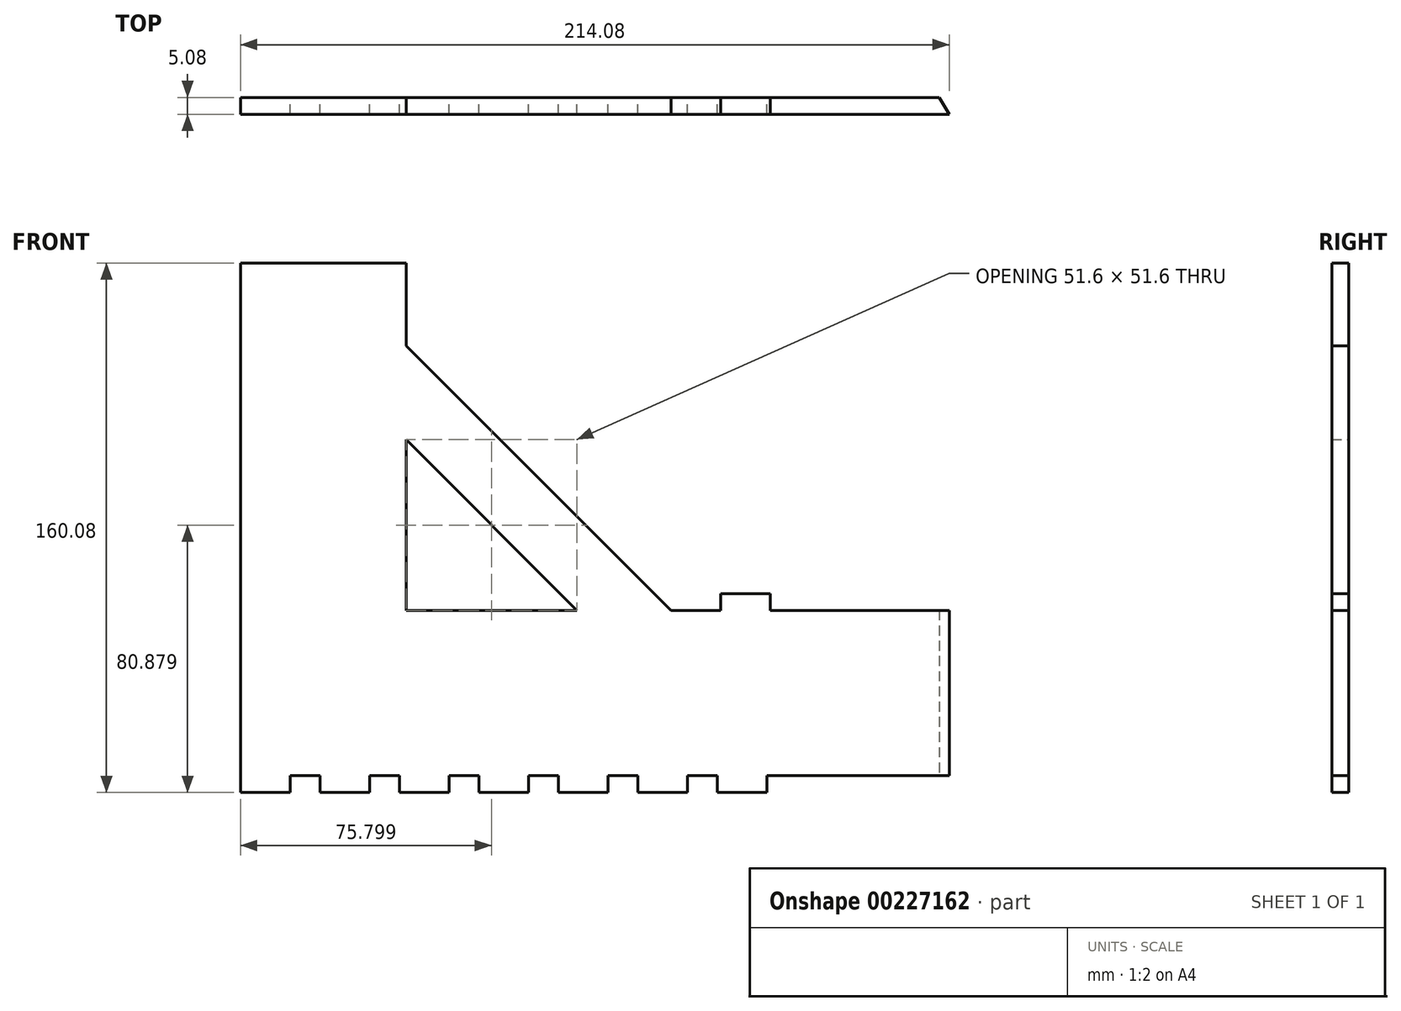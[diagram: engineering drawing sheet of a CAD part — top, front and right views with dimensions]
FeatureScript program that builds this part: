
annotation { "Feature Type Name" : "Feature", "Feature Type Description" : "" }
export const myFeature = defineFeature(function(context is Context, id is Id, definition is map)
    precondition{}
    {
        {
            var Q0;
            Q0=qCreatedBy(makeId("Front.planeOp"),FACE);
            var sketch = newSketch(context, id + "F0", { "sketchPlane" : qUnion([Q0])});
            skLineSegment(sketch, "E0", {"start": v(-32.42, 0) * mm, "end": v(-246.5, 0) * mm});
            skLineSegment(sketch, "E1", {"start": v(-246.5, 0) * mm, "end": v(-246.5, 130) * mm});
            skLineSegment(sketch, "E2", {"start": v(-246.5, 130) * mm, "end": v(-196.5, 130) * mm});
            skLineSegment(sketch, "E3", {"start": v(-196.5, 130) * mm, "end": v(-196.5, 50) * mm});
            skLineSegment(sketch, "E4", {"start": v(-196.5, 50) * mm, "end": v(-32.42, 50) * mm});
            skLineSegment(sketch, "E5", {"start": v(-196.5, 130) * mm, "end": v(-116.5, 50) * mm});
            skLineSegment(sketch, "E6", {"start": v(-196.5, 101.6) * mm, "end": v(-144.9, 50) * mm});
            skLineSegment(sketch, "E7", {"start": v(-246.5, 0) * mm, "end": v(-246.5, -5.08) * mm});
            skLineSegment(sketch, "E8", {"start": v(-246.5, -5.08) * mm, "end": v(-231.5, -5.08) * mm});
            skLineSegment(sketch, "E9", {"start": v(-231.5, -5.08) * mm, "end": v(-231.5, 0) * mm});
            skLineSegment(sketch, "E10.1.0.0", {"start": v(-207.5, -5.08) * mm, "end": v(-207.5, 0) * mm});
            skLineSegment(sketch, "E10.1.0.1", {"start": v(-222.5, -5.08) * mm, "end": v(-207.5, -5.08) * mm});
            skLineSegment(sketch, "E10.1.0.2", {"start": v(-222.5, 0) * mm, "end": v(-222.5, -5.08) * mm});
            skLineSegment(sketch, "E10.2.0.0", {"start": v(-183.5, -5.08) * mm, "end": v(-183.5, 0) * mm});
            skLineSegment(sketch, "E10.2.0.1", {"start": v(-198.5, -5.08) * mm, "end": v(-183.5, -5.08) * mm});
            skLineSegment(sketch, "E10.2.0.2", {"start": v(-198.5, 0) * mm, "end": v(-198.5, -5.08) * mm});
            skLineSegment(sketch, "E10.3.0.0", {"start": v(-159.5, -5.08) * mm, "end": v(-159.5, 0) * mm});
            skLineSegment(sketch, "E10.3.0.1", {"start": v(-174.5, -5.08) * mm, "end": v(-159.5, -5.08) * mm});
            skLineSegment(sketch, "E10.3.0.2", {"start": v(-174.5, 0) * mm, "end": v(-174.5, -5.08) * mm});
            skLineSegment(sketch, "E10.4.0.0", {"start": v(-135.5, -5.08) * mm, "end": v(-135.5, 0) * mm});
            skLineSegment(sketch, "E10.4.0.1", {"start": v(-150.5, -5.08) * mm, "end": v(-135.5, -5.08) * mm});
            skLineSegment(sketch, "E10.4.0.2", {"start": v(-150.5, 0) * mm, "end": v(-150.5, -5.08) * mm});
            skLineSegment(sketch, "E10.5.0.0", {"start": v(-111.5, -5.08) * mm, "end": v(-111.5, 0) * mm});
            skLineSegment(sketch, "E10.5.0.1", {"start": v(-126.5, -5.08) * mm, "end": v(-111.5, -5.08) * mm});
            skLineSegment(sketch, "E10.5.0.2", {"start": v(-126.5, 0) * mm, "end": v(-126.5, -5.08) * mm});
            skLineSegment(sketch, "E10.6.0.0", {"start": v(-87.5, -5.08) * mm, "end": v(-87.5, 0) * mm});
            skLineSegment(sketch, "E10.6.0.1", {"start": v(-102.5, -5.08) * mm, "end": v(-87.5, -5.08) * mm});
            skLineSegment(sketch, "E10.6.0.2", {"start": v(-102.5, 0) * mm, "end": v(-102.5, -5.08) * mm});
            skLineSegment(sketch, "E10.direction1", {"start": v(-246.5, -5.08) * mm, "end": v(-222.5, -5.08) * mm, "construction": true});
            skLineSegment(sketch, "E11", {"start": v(-32.42, 50) * mm, "end": v(-32.42, 0) * mm});
            skPoint(sketch, "E12.start.orphan", {"position": v(0, 50) * mm});
            skSolve(sketch);
        }
        {
            var Q0;
            Q0=qSketchRegion(id+"F0",true);
            extrude(context, id + "F1", {"entities" : qUnion([Q0]), "depth" : 5.08 * mm});
        }
        {
            var Q0;
            Q0=makeQuery(id+"F1.opExtrude","SWEPT_FACE",FACE,{"disambiguationData":[OSD([sQuery(id+"F0.wireOp",EDGE,"E2")])]});
            var Q1;
            Q1=makeQuery(id+"F1.opExtrude","SWEPT_FACE",FACE,{"disambiguationData":[OSD([sQuery(id+"F0.wireOp",EDGE,"0f3f7d79-0024-4810-854d-b7a6c9fa19c64.MirrorCS")])]});
            extrude(context, id + "F2", {"entities" : qUnion([Q0, Q1]), "operationType" : NewBodyOperationType.ADD, "depth" : 25 * mm});
        }
        {
            var Q0;
            {var subQ0=sQuery(id+"F0.wireOp",EDGE,"E0");Q0=makeQuery(id+"F1.opExtrude","SWEPT_FACE",FACE,{"disambiguationData":[OSD([subQ0]),TDD([makeQuery(id+"F0.imprint","IMPRINT",EDGE,{"disambiguationData":[TD([[makeQuery(id+"F0.imprint","INTERSECT",VERTEX,{"derivedFrom":[subQ0,sQuery(id+"F0.wireOp",EDGE,"E11")]}),-1.0]])],"derivedFrom":subQ0})])]});}
            var sketch = newSketch(context, id + "F3", { "sketchPlane" : qUnion([Q0])});
            skLineSegment(sketch, "E13", {"start": v(-32.42, 5.08) * mm, "end": v(-35.35, 0) * mm});
            skSolve(sketch);
        }
        {
            var Q0;
            {var subQ0=sQuery(id+"F3.wireOp",EDGE,"E13");Q0=makeQuery(id+"F3.imprint","IMPRINT",FACE,{"disambiguationData":[TD([[makeQuery(id+"F3.imprint","IMPRINT",EDGE,{"derivedFrom":subQ0}),1.0]])]});}
            extrude(context, id + "F4", {"entities" : qUnion([Q0]), "operationType" : NewBodyOperationType.REMOVE, "oppositeDirection" : true, "depth" : 58 * mm});
        }
        {
            var Q0;
            {var subQ0=sQuery(id+"F0.wireOp",EDGE,"E4");Q0=makeQuery(id+"F1.opExtrude","SWEPT_FACE",FACE,{"disambiguationData":[OSD([subQ0]),TDD([makeQuery(id+"F0.imprint","IMPRINT",EDGE,{"disambiguationData":[TD([[makeQuery(id+"F0.imprint","INTERSECT",VERTEX,{"derivedFrom":[subQ0,sQuery(id+"F0.wireOp",EDGE,"E11")]}),1.0]])],"derivedFrom":subQ0})])]});}
            var sketch = newSketch(context, id + "F5", { "sketchPlane" : qUnion([Q0])});
            skLineSegment(sketch, "E14.right", {"start": v(-101.5, 0) * mm, "end": v(-101.5, -5.08) * mm});
            skLineSegment(sketch, "E15.MirrorCS", {"start": v(-86.5, 0) * mm, "end": v(-86.5, -5.08) * mm});
            skPoint(sketch, "E14.top.start.orphan", {"position": v(-116.5, -5.08) * mm});
            skPoint(sketch, "E14.bottom.start.orphan", {"position": v(-116.5, 0) * mm});
            skLineSegment(sketch, "E16", {"start": v(-101.5, 0) * mm, "end": v(-86.5, 0) * mm});
            skLineSegment(sketch, "E17", {"start": v(-86.5, -5.08) * mm, "end": v(-101.5, -5.08) * mm});
            skSolve(sketch);
        }
        {
            var Q0;
            Q0 = qSketchRegion(id + "F5", true);
            extrude(context, id + "F6", {"entities" : qUnion([Q0]), "operationType" : NewBodyOperationType.ADD, "depth" : 5.08 * mm});
        }
    });
